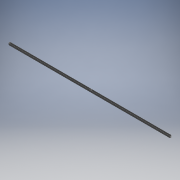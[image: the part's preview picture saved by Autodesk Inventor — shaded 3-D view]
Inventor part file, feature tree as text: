
AUTODESK INVENTOR PART (.ipt)
format: ipt  version: 2017.3 (Build 213256000, 256)  size: 147,456 bytes
history: native  units: mm (DEFAULTED — no unit token found)
features: extrude x2
ambient origin geometry x8: Origin, YZ Plane, XZ Plane, XY Plane, X Axis, Y Axis, Z Axis, Center Point
bodies: Solid1 (feature_tree)
feature tree (2):
  extrude  "Extrusion1"  Depth=9.0mm TaperAngle=0.0deg
  extrude  "Extrusion2"  Depth=9.0mm TaperAngle=0.0deg
